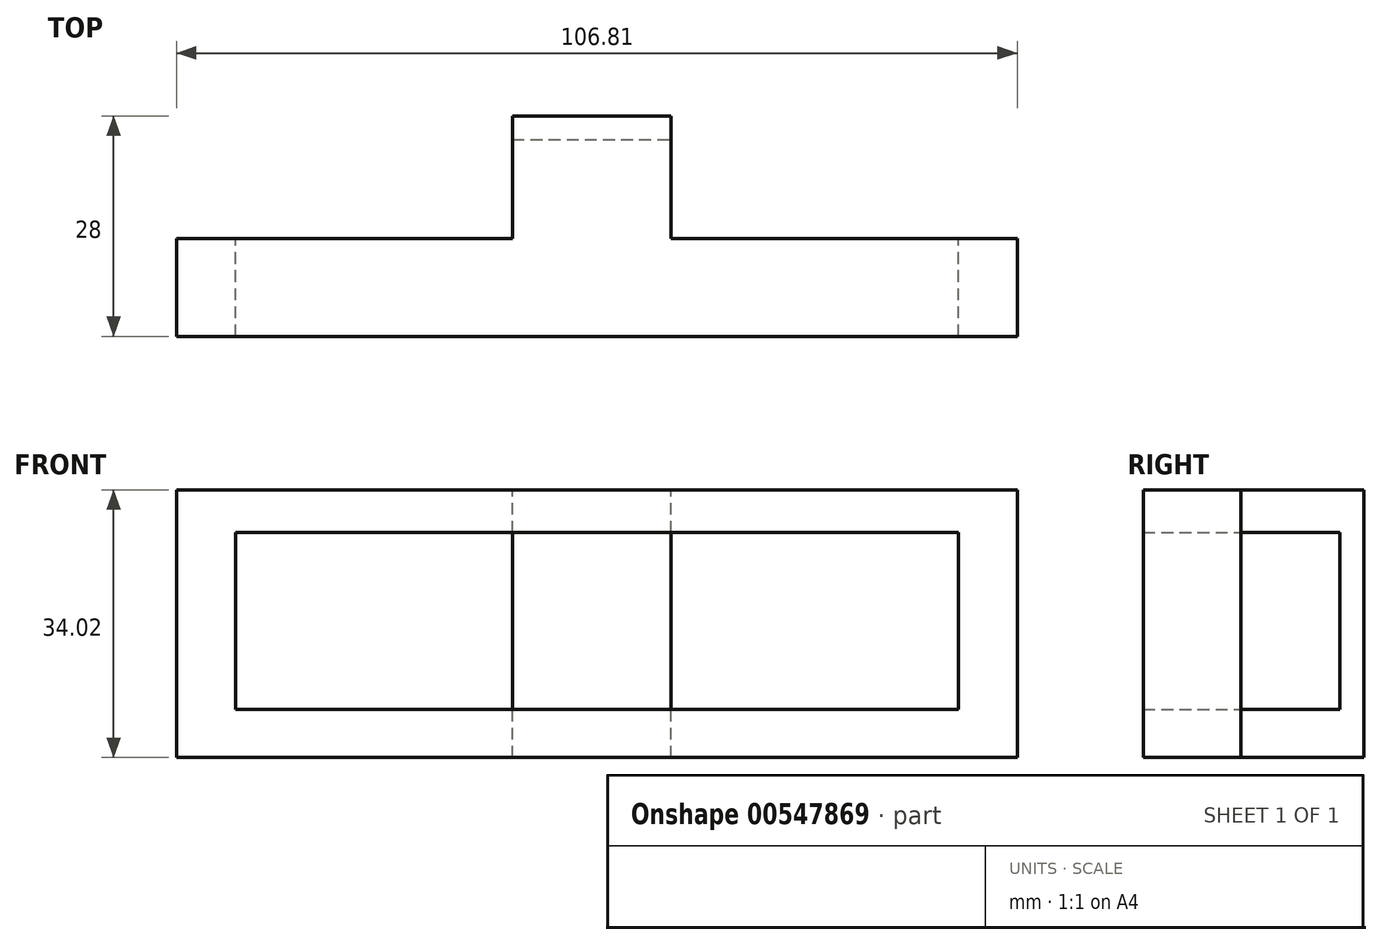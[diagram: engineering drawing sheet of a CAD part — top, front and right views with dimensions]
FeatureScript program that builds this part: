
annotation { "Feature Type Name" : "Feature", "Feature Type Description" : "" }
export const myFeature = defineFeature(function(context is Context, id is Id, definition is map)
    precondition{}
    {
        {
            var Q0;
            Q0=qCreatedBy(makeId("Front.planeOp"),FACE);
            var sketch = newSketch(context, id + "F0", { "sketchPlane" : qUnion([Q0])});
            skLineSegment(sketch, "E0.bottom", {"start": v(-48.81, 17.35) * mm, "end": v(58, 17.35) * mm});
            skLineSegment(sketch, "E0.top", {"start": v(-48.81, -16.67) * mm, "end": v(58, -16.67) * mm});
            skLineSegment(sketch, "E0.left", {"start": v(-48.81, 17.35) * mm, "end": v(-48.81, -16.67) * mm});
            skLineSegment(sketch, "E0.right", {"start": v(58, 17.35) * mm, "end": v(58, -16.67) * mm});
            skLineSegment(sketch, "E1.bottom", {"start": v(-41.33, 11.9) * mm, "end": v(50.52, 11.9) * mm});
            skLineSegment(sketch, "E1.top", {"start": v(-41.33, -10.55) * mm, "end": v(50.52, -10.55) * mm});
            skLineSegment(sketch, "E1.left", {"start": v(-41.33, 11.9) * mm, "end": v(-41.33, -10.55) * mm});
            skLineSegment(sketch, "E1.right", {"start": v(50.52, 11.9) * mm, "end": v(50.52, -10.55) * mm});
            skSolve(sketch);
        }
        {
            var Q0;
            Q0=makeQuery(id+"F0.imprint","IMPRINT",FACE,{"disambiguationData":[TD([[makeQuery(id+"F0.imprint","IMPRINT",EDGE,{"derivedFrom":sQuery(id+"F0.wireOp",EDGE,"E0.bottom")}),-1.0]])]});
            extrude(context, id + "F1", {"entities" : qUnion([Q0]), "depth" : 25 * mm, "offsetDistance" : 25 * mm});
        }
        {
            var Q0;
            Q0=makeQuery(id+"F1.opExtrude","CAP_FACE",FACE,{"disambiguationData":[OSD([sQuery(id+"F0.wireOp",EDGE,"E0.bottom"),sQuery(id+"F0.wireOp",EDGE,"E0.top"),sQuery(id+"F0.wireOp",EDGE,"E0.left"),sQuery(id+"F0.wireOp",EDGE,"E0.right"),sQuery(id+"F0.wireOp",EDGE,"E1.bottom"),sQuery(id+"F0.wireOp",EDGE,"E1.top"),sQuery(id+"F0.wireOp",EDGE,"E1.left"),sQuery(id+"F0.wireOp",EDGE,"E1.right")])],"isStart":true});
            var sketch = newSketch(context, id + "F2", { "sketchPlane" : qUnion([Q0])});
            skLineSegment(sketch, "E2.bottom", {"start": v(48.81, 17.35) * mm, "end": v(-58, 17.35) * mm});
            skLineSegment(sketch, "E2.top", {"start": v(48.81, -16.67) * mm, "end": v(-58, -16.67) * mm});
            skLineSegment(sketch, "E2.left", {"start": v(48.81, 17.35) * mm, "end": v(48.81, -16.67) * mm});
            skLineSegment(sketch, "E2.right", {"start": v(-58, 17.35) * mm, "end": v(-58, -16.67) * mm});
            skSolve(sketch);
        }
        {
            var Q0;
            Q0 = qSketchRegion(id + "F2", true);
            extrude(context, id + "F3", {"entities" : qUnion([Q0]), "operationType" : NewBodyOperationType.ADD, "depth" : 3 * mm, "offsetDistance" : 25 * mm});
        }
        {
            var Q0;
            Q0=makeQuery(id+"F3.boolean.opBoolean","MERGE",FACE,{"derivedFrom":[makeQuery(id+"F1.opExtrude","SWEPT_FACE",FACE,{"disambiguationData":[OSD([sQuery(id+"F0.wireOp",EDGE,"E0.bottom")])]}),makeQuery(id+"F3.opExtrude","SWEPT_FACE",FACE,{"disambiguationData":[OSD([sQuery(id+"F2.wireOp",EDGE,"E2.bottom")])]})]});
            var sketch = newSketch(context, id + "F4", { "sketchPlane" : qUnion([Q0])});
            skLineSegment(sketch, "E3.bottom", {"start": v(13.98, 11.48) * mm, "end": v(73.17, 11.48) * mm});
            skLineSegment(sketch, "E3.top", {"start": v(13.98, -12.6) * mm, "end": v(73.17, -12.6) * mm});
            skLineSegment(sketch, "E3.left", {"start": v(13.98, 11.48) * mm, "end": v(13.98, -12.6) * mm});
            skLineSegment(sketch, "E3.right", {"start": v(73.17, 11.48) * mm, "end": v(73.17, -12.6) * mm});
            skLineSegment(sketch, "E4.bottom", {"start": v(-62.21, 15.73) * mm, "end": v(-6.13, 15.73) * mm});
            skLineSegment(sketch, "E4.top", {"start": v(-62.21, -12.6) * mm, "end": v(-6.13, -12.6) * mm});
            skLineSegment(sketch, "E4.left", {"start": v(-62.21, 15.73) * mm, "end": v(-62.21, -12.6) * mm});
            skLineSegment(sketch, "E4.right", {"start": v(-6.13, 15.73) * mm, "end": v(-6.13, -12.6) * mm});
            skSolve(sketch);
        }
        {
            var Q0;
            {var subQ0=sQuery(id+"F4.wireOp",EDGE,"E4.right");var subQ1=sQuery(id+"F4.wireOp",EDGE,"E4.top");var subQ2=makeQuery(id+"F4.imprint","INTERSECT",VERTEX,{"derivedFrom":[subQ1,subQ0]});Q0=makeQuery(id+"F4.imprint","IMPRINT",FACE,{"disambiguationData":[TD([[makeQuery(id+"F4.imprint","IMPRINT",EDGE,{"disambiguationData":[TD([[subQ2,1.0]])],"derivedFrom":subQ0}),-1.0]])]});}
            var Q1;
            {var subQ0=sQuery(id+"F4.wireOp",EDGE,"E3.left");var subQ1=sQuery(id+"F4.wireOp",EDGE,"E3.top");var subQ2=makeQuery(id+"F4.imprint","INTERSECT",VERTEX,{"derivedFrom":[subQ1,subQ0]});Q1=makeQuery(id+"F4.imprint","IMPRINT",FACE,{"disambiguationData":[TD([[makeQuery(id+"F4.imprint","IMPRINT",EDGE,{"disambiguationData":[TD([[subQ2,1.0]])],"derivedFrom":subQ0}),1.0]])]});}
            extrude(context, id + "F5", {"entities" : qUnion([Q0, Q1]), "operationType" : NewBodyOperationType.REMOVE, "oppositeDirection" : true, "depth" : 42.7 * mm, "offsetDistance" : 25 * mm});
        }
    });
